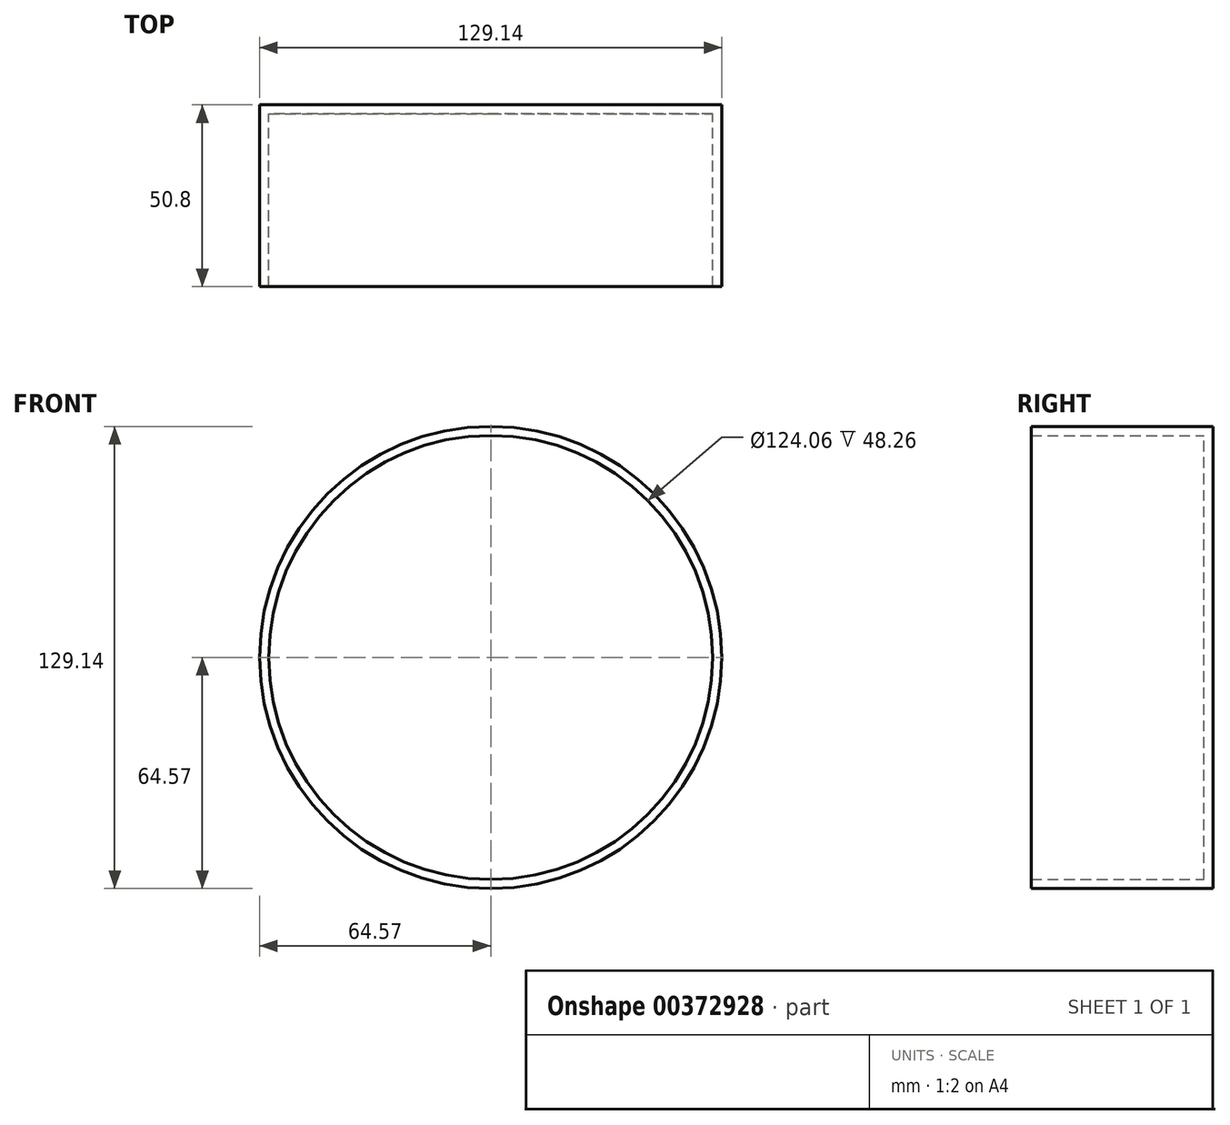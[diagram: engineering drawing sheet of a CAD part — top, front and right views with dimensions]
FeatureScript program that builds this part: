
annotation { "Feature Type Name" : "Feature", "Feature Type Description" : "" }
export const myFeature = defineFeature(function(context is Context, id is Id, definition is map)
    precondition{}
    {
        {
            var Q0;
            Q0=qCreatedBy(makeId("Front.planeOp"),FACE);
            var sketch = newSketch(context, id + "F0", { "sketchPlane" : qUnion([Q0])});
            skCircle(sketch, "E0", {"center": v(0, 0) * mm, "radius": 64.57 * mm});
            skSolve(sketch);
        }
        {
            var Q0;
            Q0=makeQuery(id+"F0.imprint","IMPRINT",FACE,{"disambiguationData":[TD([[makeQuery(id+"F0.imprint","IMPRINT",EDGE,{"derivedFrom":sQuery(id+"F0.wireOp",EDGE,"E0")}),1.0]])]});
            var sketch = newSketch(context, id + "F1", { "sketchPlane" : qUnion([Q0])});
            skSolve(sketch);
        }
        {
            var Q0;
            Q0=makeQuery(id+"F1.imprint","IMPRINT",FACE,{"disambiguationData":[TD([[makeQuery(id+"F1.imprint","IMPRINT",EDGE,{"derivedFrom":makeQuery(id+"F0.imprint","IMPRINT",EDGE,{"derivedFrom":sQuery(id+"F0.wireOp",EDGE,"E0")})}),1.0]])]});
            var sketch = newSketch(context, id + "F2", { "sketchPlane" : qUnion([Q0])});
            skSolve(sketch);
        }
        {
            var Q0;
            Q0=makeQuery(id+"F2.imprint","IMPRINT",FACE,{"disambiguationData":[TD([[makeQuery(id+"F2.imprint","IMPRINT",EDGE,{"derivedFrom":makeQuery(id+"F1.imprint","IMPRINT",EDGE,{"derivedFrom":makeQuery(id+"F0.imprint","IMPRINT",EDGE,{"derivedFrom":sQuery(id+"F0.wireOp",EDGE,"E0")})})}),1.0]])]});
            extrude(context, id + "F3", {"entities" : qUnion([Q0]), "depth" : 25.4 * mm});
        }
        {
            var Q0;
            Q0=makeQuery(id+"F3.opExtrude","CAP_FACE",FACE,{"disambiguationData":[OSD([sQuery(id+"F0.wireOp",EDGE,"E0")])],"isStart":false});
            extrude(context, id + "F4", {"entities" : qUnion([Q0]), "operationType" : NewBodyOperationType.ADD, "depth" : 25.4 * mm});
        }
        {
            var Q0;
            Q0=makeQuery(id+"F4.opExtrude","CAP_FACE",FACE,{"disambiguationData":[OSD([sQuery(id+"F0.wireOp",EDGE,"E0")])],"isStart":false});
            shell(context, id + "F5", {"entities" : qUnion([Q0]), "thickness" : 2.54 * mm});
        }
    });
